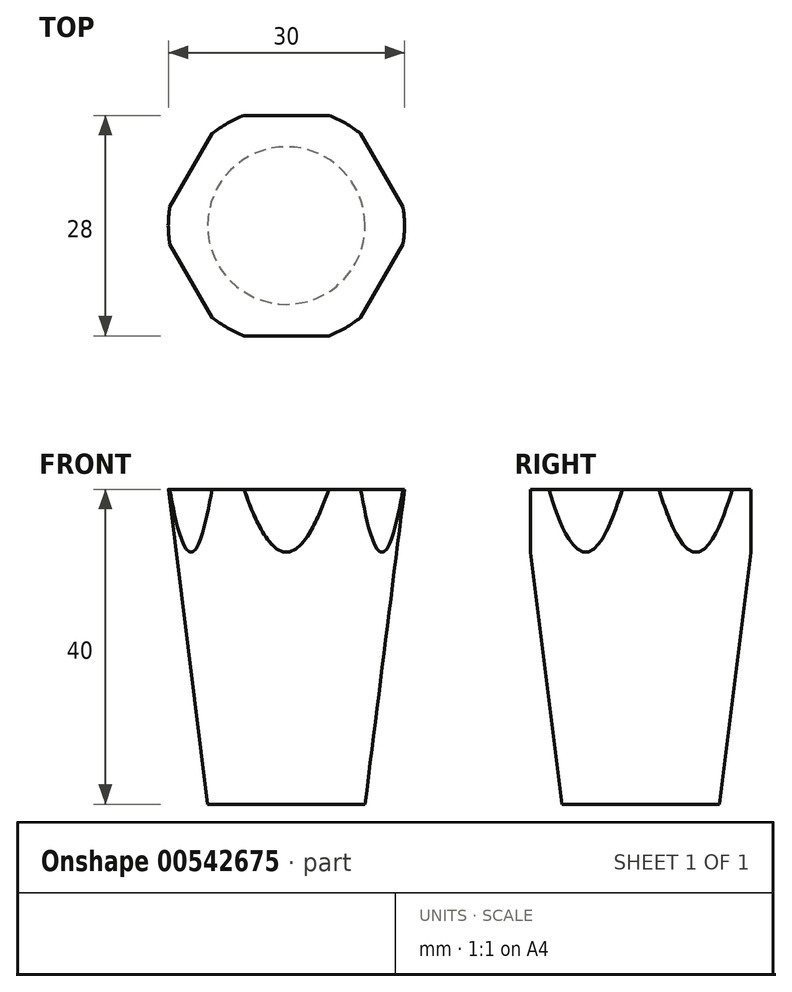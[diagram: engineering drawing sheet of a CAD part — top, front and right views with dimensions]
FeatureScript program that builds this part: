
annotation { "Feature Type Name" : "Feature", "Feature Type Description" : "" }
export const myFeature = defineFeature(function(context is Context, id is Id, definition is map)
    precondition{}
    {
        {
            var Q0;
            Q0=qCreatedBy(makeId("Front.planeOp"),FACE);
            var sketch = newSketch(context, id + "F0", { "sketchPlane" : qUnion([Q0])});
            skLineSegment(sketch, "E0", {"start": v(0, 0) * mm, "end": v(-10, 0) * mm});
            skLineSegment(sketch, "E1", {"start": v(-10, 0) * mm, "end": v(-15, 40) * mm});
            skLineSegment(sketch, "E2", {"start": v(-15, 40) * mm, "end": v(0, 40) * mm});
            skLineSegment(sketch, "E3", {"start": v(0, 40) * mm, "end": v(0, 0) * mm});
            skSolve(sketch);
        }
        {
            var Q0;
            Q0=makeQuery(id+"F0.imprint","IMPRINT",FACE,{"disambiguationData":[TD([[makeQuery(id+"F0.imprint","IMPRINT",EDGE,{"derivedFrom":sQuery(id+"F0.wireOp",EDGE,"E0")}),-1.0]])]});
            var Q1;
            Q1=sQuery(id+"F0.wireOp",EDGE,"E3");
            revolve(context, id + "F1", {"entities" : qUnion([Q0]), "axis" : qUnion([Q1]), "revolveType" : RevolveType.FULL});
        }
        {
            var Q0;
            Q0=makeQuery(id+"F1.opRevolve","SWEPT_FACE",FACE,{"disambiguationData":[OSD([sQuery(id+"F0.wireOp",EDGE,"E2")])]});
            var sketch = newSketch(context, id + "F2", { "sketchPlane" : qUnion([Q0])});
            skLineSegment(sketch, "E4.bottom", {"start": v(6, 16) * mm, "end": v(-6, 16) * mm});
            skLineSegment(sketch, "E4.top", {"start": v(6, 14) * mm, "end": v(-6, 14) * mm});
            skLineSegment(sketch, "E4.left", {"start": v(6, 16) * mm, "end": v(6, 14) * mm});
            skLineSegment(sketch, "E4.right", {"start": v(-6, 16) * mm, "end": v(-6, 14) * mm});
            skPoint(sketch, "E4.middle", {"position": v(0, 15) * mm});
            skPoint(sketch, "E5.1.0", {"position": v(-13, 7.5) * mm});
            skLineSegment(sketch, "E5.1.1", {"start": v(-10.86, 13.2) * mm, "end": v(-16.86, 2.8) * mm});
            skLineSegment(sketch, "E5.1.2", {"start": v(-9.12, 12.2) * mm, "end": v(-15.12, 1.8) * mm});
            skLineSegment(sketch, "E5.1.3", {"start": v(-10.86, 13.2) * mm, "end": v(-9.12, 12.2) * mm});
            skLineSegment(sketch, "E5.1.4", {"start": v(-16.86, 2.8) * mm, "end": v(-15.12, 1.8) * mm});
            skPoint(sketch, "E5.2.0", {"position": v(-13, -7.5) * mm});
            skLineSegment(sketch, "E5.2.1", {"start": v(-16.86, -2.8) * mm, "end": v(-10.86, -13.2) * mm});
            skLineSegment(sketch, "E5.2.2", {"start": v(-15.12, -1.8) * mm, "end": v(-9.12, -12.2) * mm});
            skLineSegment(sketch, "E5.2.3", {"start": v(-16.86, -2.8) * mm, "end": v(-15.12, -1.8) * mm});
            skLineSegment(sketch, "E5.2.4", {"start": v(-10.86, -13.2) * mm, "end": v(-9.12, -12.2) * mm});
            skPoint(sketch, "E5.3.0", {"position": v(0, -15) * mm});
            skLineSegment(sketch, "E5.3.1", {"start": v(-6, -16) * mm, "end": v(6, -16) * mm});
            skLineSegment(sketch, "E5.3.2", {"start": v(-6, -14) * mm, "end": v(6, -14) * mm});
            skLineSegment(sketch, "E5.3.3", {"start": v(-6, -16) * mm, "end": v(-6, -14) * mm});
            skLineSegment(sketch, "E5.3.4", {"start": v(6, -16) * mm, "end": v(6, -14) * mm});
            skPoint(sketch, "E5.4.0", {"position": v(13, -7.5) * mm});
            skLineSegment(sketch, "E5.4.1", {"start": v(10.86, -13.2) * mm, "end": v(16.86, -2.8) * mm});
            skLineSegment(sketch, "E5.4.2", {"start": v(9.12, -12.2) * mm, "end": v(15.12, -1.8) * mm});
            skLineSegment(sketch, "E5.4.3", {"start": v(10.86, -13.2) * mm, "end": v(9.12, -12.2) * mm});
            skLineSegment(sketch, "E5.4.4", {"start": v(16.86, -2.8) * mm, "end": v(15.12, -1.8) * mm});
            skPoint(sketch, "E5.5.0", {"position": v(13, 7.5) * mm});
            skLineSegment(sketch, "E5.5.1", {"start": v(16.86, 2.8) * mm, "end": v(10.86, 13.2) * mm});
            skLineSegment(sketch, "E5.5.2", {"start": v(15.12, 1.8) * mm, "end": v(9.12, 12.2) * mm});
            skLineSegment(sketch, "E5.5.3", {"start": v(16.86, 2.8) * mm, "end": v(15.12, 1.8) * mm});
            skLineSegment(sketch, "E5.5.4", {"start": v(10.86, 13.2) * mm, "end": v(9.12, 12.2) * mm});
            skPoint(sketch, "E5.center", {"position": v(0, 0) * mm});
            skSolve(sketch);
        }
        {
            var Q0;
            {var subQ0=sQuery(id+"F2.wireOp",EDGE,"E5.2.2");var subQ1=makeQuery(id+"F1.opRevolve","SWEPT_EDGE",EDGE,{"disambiguationData":[OSD([sQuery(id+"F0.wireOp",EDGE,"E1"),sQuery(id+"F0.wireOp",EDGE,"E2")])]});var subQ2=makeQuery(id+"F2.imprint","INTERSECT",VERTEX,{"disambiguationData":[OD(0.0)],"derivedFrom":[subQ1,subQ0]});Q0=makeQuery(id+"F2.imprint","IMPRINT",FACE,{"disambiguationData":[TD([[makeQuery(id+"F2.imprint","IMPRINT",EDGE,{"disambiguationData":[TD([[subQ2,-1.0]])],"derivedFrom":subQ0}),-1.0]])]});}
            var Q1;
            {var subQ0=sQuery(id+"F2.wireOp",EDGE,"E5.1.2");var subQ1=makeQuery(id+"F1.opRevolve","SWEPT_EDGE",EDGE,{"disambiguationData":[OSD([sQuery(id+"F0.wireOp",EDGE,"E1"),sQuery(id+"F0.wireOp",EDGE,"E2")])]});var subQ2=makeQuery(id+"F2.imprint","INTERSECT",VERTEX,{"disambiguationData":[OD(0.0)],"derivedFrom":[subQ1,subQ0]});Q1=makeQuery(id+"F2.imprint","IMPRINT",FACE,{"disambiguationData":[TD([[makeQuery(id+"F2.imprint","IMPRINT",EDGE,{"disambiguationData":[TD([[subQ2,-1.0]])],"derivedFrom":subQ0}),-1.0]])]});}
            var Q2;
            {var subQ0=sQuery(id+"F2.wireOp",EDGE,"E4.top");var subQ1=makeQuery(id+"F1.opRevolve","SWEPT_EDGE",EDGE,{"disambiguationData":[OSD([sQuery(id+"F0.wireOp",EDGE,"E1"),sQuery(id+"F0.wireOp",EDGE,"E2")])]});var subQ2=makeQuery(id+"F2.imprint","INTERSECT",VERTEX,{"disambiguationData":[OD(0.0)],"derivedFrom":[subQ1,subQ0]});Q2=makeQuery(id+"F2.imprint","IMPRINT",FACE,{"disambiguationData":[TD([[makeQuery(id+"F2.imprint","IMPRINT",EDGE,{"disambiguationData":[TD([[subQ2,-1.0]])],"derivedFrom":subQ0}),-1.0]])]});}
            var Q3;
            {var subQ0=sQuery(id+"F2.wireOp",EDGE,"E5.5.2");var subQ1=makeQuery(id+"F1.opRevolve","SWEPT_EDGE",EDGE,{"disambiguationData":[OSD([sQuery(id+"F0.wireOp",EDGE,"E1"),sQuery(id+"F0.wireOp",EDGE,"E2")])]});var subQ2=makeQuery(id+"F2.imprint","INTERSECT",VERTEX,{"disambiguationData":[OD(0.0)],"derivedFrom":[subQ1,subQ0]});Q3=makeQuery(id+"F2.imprint","IMPRINT",FACE,{"disambiguationData":[TD([[makeQuery(id+"F2.imprint","IMPRINT",EDGE,{"disambiguationData":[TD([[subQ2,-1.0]])],"derivedFrom":subQ0}),-1.0]])]});}
            var Q4;
            {var subQ0=sQuery(id+"F2.wireOp",EDGE,"E5.4.2");var subQ1=makeQuery(id+"F1.opRevolve","SWEPT_EDGE",EDGE,{"disambiguationData":[OSD([sQuery(id+"F0.wireOp",EDGE,"E1"),sQuery(id+"F0.wireOp",EDGE,"E2")])]});var subQ2=makeQuery(id+"F2.imprint","INTERSECT",VERTEX,{"disambiguationData":[OD(0.0)],"derivedFrom":[subQ1,subQ0]});Q4=makeQuery(id+"F2.imprint","IMPRINT",FACE,{"disambiguationData":[TD([[makeQuery(id+"F2.imprint","IMPRINT",EDGE,{"disambiguationData":[TD([[subQ2,-1.0]])],"derivedFrom":subQ0}),-1.0]])]});}
            var Q5;
            {var subQ0=sQuery(id+"F2.wireOp",EDGE,"E5.3.2");var subQ1=makeQuery(id+"F1.opRevolve","SWEPT_EDGE",EDGE,{"disambiguationData":[OSD([sQuery(id+"F0.wireOp",EDGE,"E1"),sQuery(id+"F0.wireOp",EDGE,"E2")])]});var subQ2=makeQuery(id+"F2.imprint","INTERSECT",VERTEX,{"disambiguationData":[OD(0.0)],"derivedFrom":[subQ1,subQ0]});Q5=makeQuery(id+"F2.imprint","IMPRINT",FACE,{"disambiguationData":[TD([[makeQuery(id+"F2.imprint","IMPRINT",EDGE,{"disambiguationData":[TD([[subQ2,-1.0]])],"derivedFrom":subQ0}),-1.0]])]});}
            extrude(context, id + "F3", {"entities" : qUnion([Q0, Q1, Q2, Q3, Q4, Q5]), "operationType" : NewBodyOperationType.REMOVE, "oppositeDirection" : true, "depth" : 10 * mm, "offsetDistance" : 25 * mm});
        }
    });
